# Revit family: P710093-031
name_source: partatom
category: Lighting Fixtures
revit_build: Autodesk Revit 2014 (Build: 20130308_1515(x64)
units: mm (PartAtom-declared; Revit-internal decimal feet)

## types (1)
- P710093-031
    Apparent Load = 17 VA
    Assembly Code = D5020200
    Color Filter = 16777215
    Connector Description = Lighting Connector
    Default Elevation = 48"
    Depth = 3 7/8"
    Description = Create an extension of your personality and lifestyle with the rustic charm of the wall bracket. Country character is the cornerstone of this light fixture with an aged oak finish. The design is completed by barn-inspired metal details.
    Dimming Lamp Color Temperature Shift = <None>
    Fixture distribution = Direct
    Glass = Paint - Hubbell - White Texture
    Gold = Hubbell - Gold
    Height = 16 3/4"
    Housing Material = Paint - Hubbell - Textured Camera Black
    Lamp = LED or Incandescent
    Load Classification = Lighting
    Manufacturer = Progress Lighting
    Model = P710093-031
    Photometric Web File = generic
    Power Factor = 1
    Product Documentation Link = https://hubbellcdn.com
    Product Link = https://www.hubbell.com
    Specifications = Country character is the cornerstone of this light fixture with an aged oak finish.
The design is completed by barn-inspired metal details.
Create an extension of your personality and lifestyle with the rustic charm of this wall light.
Ideal for any hallway, foyer, bathroom, sitting room, living room, or stairway.
Perfect for urban industrial, rustic, farmhouse, or coastal settings.
Measures 4-3/4-inch width by 16-3/4-inch height.
Uses one medium base bulb that is sold separately (60w max - LED or incandescent).
Able to be fully dimmable with dimmable bulbs.
Includes installation instructions and mounting hardware.
Progress Lighting products are designed for exceptional quality, reliability, and functionality.
    Tilt Angle = 60.00°
    URL = https://www.hubbell.com
    Voltage = 120 V
    Warranty = 1 year Warranty
    Wattage Comments = 60w
    Watts = 17 W
    White = Paint - Hubbell - Matte White
    Width = 4 3/4"
    Wood = Paint - Hubbell - Textured Camera Black

## geometry (parser evidence)
native form markers: Sweep x2
no freeform markers — native parametric forms only
